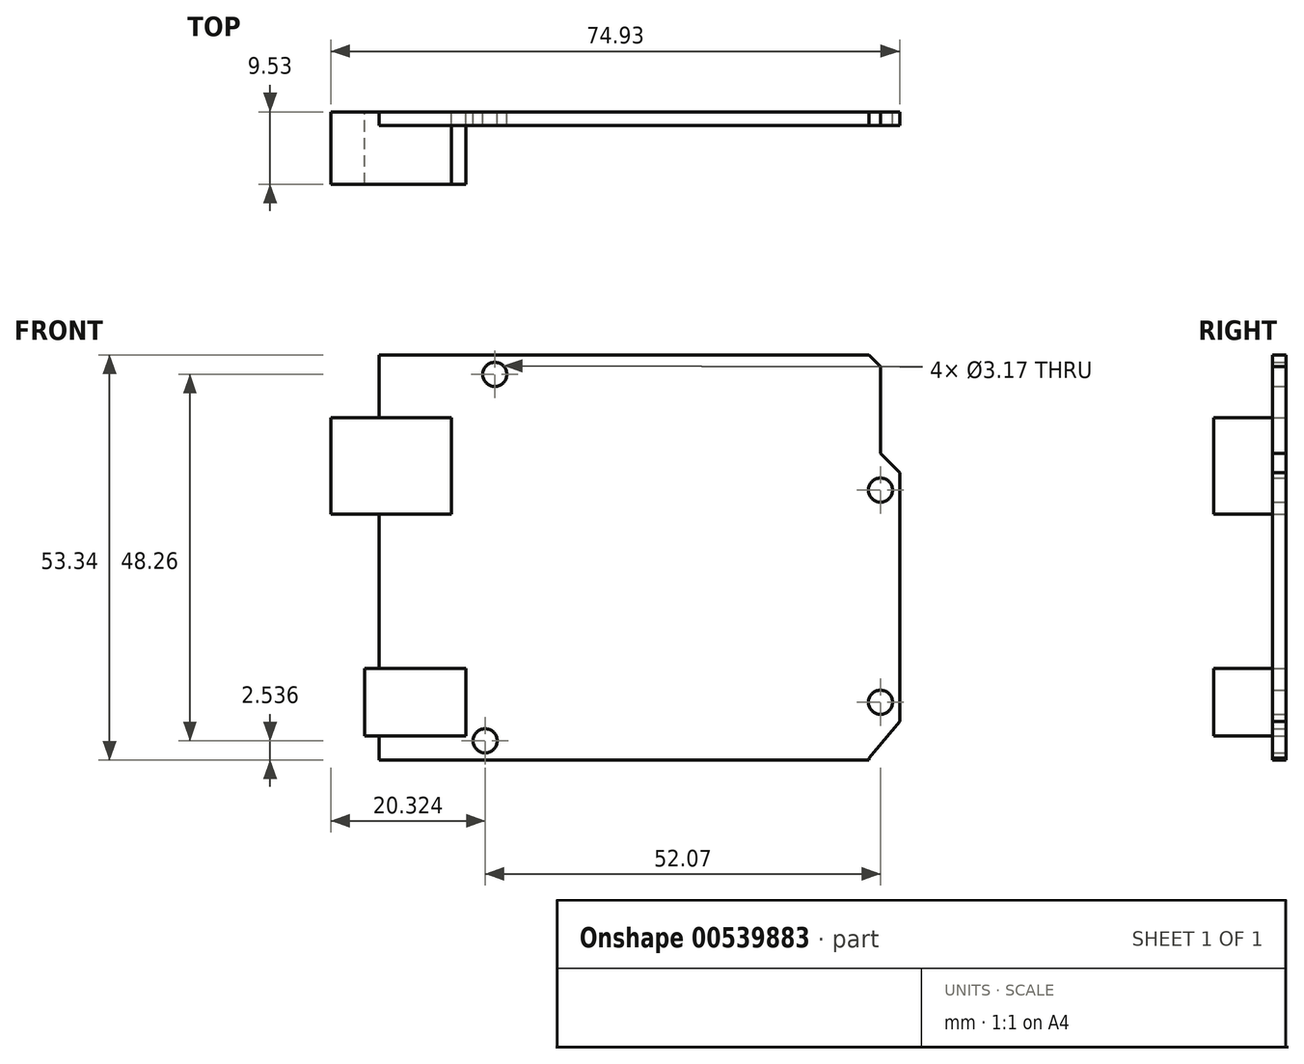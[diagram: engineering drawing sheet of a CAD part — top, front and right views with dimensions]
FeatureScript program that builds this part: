
annotation { "Feature Type Name" : "Feature", "Feature Type Description" : "" }
export const myFeature = defineFeature(function(context is Context, id is Id, definition is map)
    precondition{}
    {
        {
            var Q0;
            Q0=qCreatedBy(makeId("Front.planeOp"),FACE);
            var sketch = newSketch(context, id + "F0", { "sketchPlane" : qUnion([Q0])});
            skLineSegment(sketch, "E0", {"start": v(-48.87, 58.15) * mm, "end": v(15.66, 58.15) * mm});
            skLineSegment(sketch, "E1", {"start": v(-48.87, 58.15) * mm, "end": v(-48.87, 4.8) * mm});
            skLineSegment(sketch, "E2", {"start": v(-48.87, 4.8) * mm, "end": v(15.65, 4.8) * mm});
            skPoint(sketch, "E3", {"position": v(17.17, 12.43) * mm});
            skLineSegment(sketch, "E4", {"start": v(15.65, 4.8) * mm, "end": v(15.65, 5.04) * mm});
            skLineSegment(sketch, "E5", {"start": v(19.71, 42.65) * mm, "end": v(19.71, 9.89) * mm});
            skLineSegment(sketch, "E6", {"start": v(19.71, 9.89) * mm, "end": v(15.65, 5.04) * mm});
            skLineSegment(sketch, "E7", {"start": v(19.71, 42.65) * mm, "end": v(17.17, 45.2) * mm});
            skLineSegment(sketch, "E8", {"start": v(15.66, 58.15) * mm, "end": v(17.17, 56.62) * mm});
            skLineSegment(sketch, "E9", {"start": v(17.17, 45.2) * mm, "end": v(17.17, 56.62) * mm});
            skCircle(sketch, "E10", {"center": v(-34.9, 7.35) * mm, "radius": 1.59 * mm});
            skCircle(sketch, "E11", {"center": v(17.17, 40.37) * mm, "radius": 1.59 * mm});
            skCircle(sketch, "E12", {"center": v(17.17, 12.43) * mm, "radius": 1.59 * mm});
            skLineSegment(sketch, "E13.bottom", {"start": v(-39.34, 37.2) * mm, "end": v(-55.22, 37.2) * mm});
            skLineSegment(sketch, "E13.top", {"start": v(-39.34, 49.9) * mm, "end": v(-55.22, 49.9) * mm});
            skLineSegment(sketch, "E13.left", {"start": v(-39.34, 37.2) * mm, "end": v(-39.34, 49.9) * mm});
            skLineSegment(sketch, "E13.right", {"start": v(-55.22, 37.2) * mm, "end": v(-55.22, 49.9) * mm});
            skLineSegment(sketch, "E14.bottom", {"start": v(-50.77, 16.87) * mm, "end": v(-37.44, 16.87) * mm});
            skLineSegment(sketch, "E14.top", {"start": v(-50.77, 7.98) * mm, "end": v(-37.44, 7.98) * mm});
            skLineSegment(sketch, "E14.left", {"start": v(-50.77, 16.87) * mm, "end": v(-50.77, 7.98) * mm});
            skLineSegment(sketch, "E14.right", {"start": v(-37.44, 16.87) * mm, "end": v(-37.44, 7.98) * mm});
            skCircle(sketch, "E15", {"center": v(-33.63, 55.6) * mm, "radius": 1.59 * mm});
            skSolve(sketch);
        }
        {
            var Q0;
            {var subQ1=sQuery(id+"F0.wireOp",EDGE,"E0");Q0=makeQuery(id+"F0.imprint","IMPRINT",FACE,{"disambiguationData":[TD([[makeQuery(id+"F0.imprint","IMPRINT",EDGE,{"derivedFrom":subQ1}),-1.0]])]});}
            extrude(context, id + "F1", {"entities" : qUnion([Q0]), "depth" : 1.78 * mm, "offsetDistance" : 25.4 * mm});
        }
        {
            var Q0;
            {var subQ5=sQuery(id+"F0.wireOp",EDGE,"E13.right");Q0=makeQuery(id+"F0.imprint","IMPRINT",FACE,{"disambiguationData":[TD([[makeQuery(id+"F0.imprint","IMPRINT",EDGE,{"derivedFrom":subQ5}),-1.0]])]});}
            var Q1;
            {var subQ5=sQuery(id+"F0.wireOp",EDGE,"E13.left");Q1=makeQuery(id+"F0.imprint","IMPRINT",FACE,{"disambiguationData":[TD([[makeQuery(id+"F0.imprint","IMPRINT",EDGE,{"derivedFrom":subQ5}),1.0]])]});}
            var Q2;
            {var subQ5=sQuery(id+"F0.wireOp",EDGE,"E14.right");Q2=makeQuery(id+"F0.imprint","IMPRINT",FACE,{"disambiguationData":[TD([[makeQuery(id+"F0.imprint","IMPRINT",EDGE,{"derivedFrom":subQ5}),-1.0]])]});}
            var Q3;
            {var subQ5=sQuery(id+"F0.wireOp",EDGE,"E14.left");Q3=makeQuery(id+"F0.imprint","IMPRINT",FACE,{"disambiguationData":[TD([[makeQuery(id+"F0.imprint","IMPRINT",EDGE,{"derivedFrom":subQ5}),1.0]])]});}
            extrude(context, id + "F2", {"entities" : qUnion([Q0, Q1, Q2, Q3]), "depth" : 9.52 * mm, "offsetDistance" : 25.4 * mm});
        }
    });
